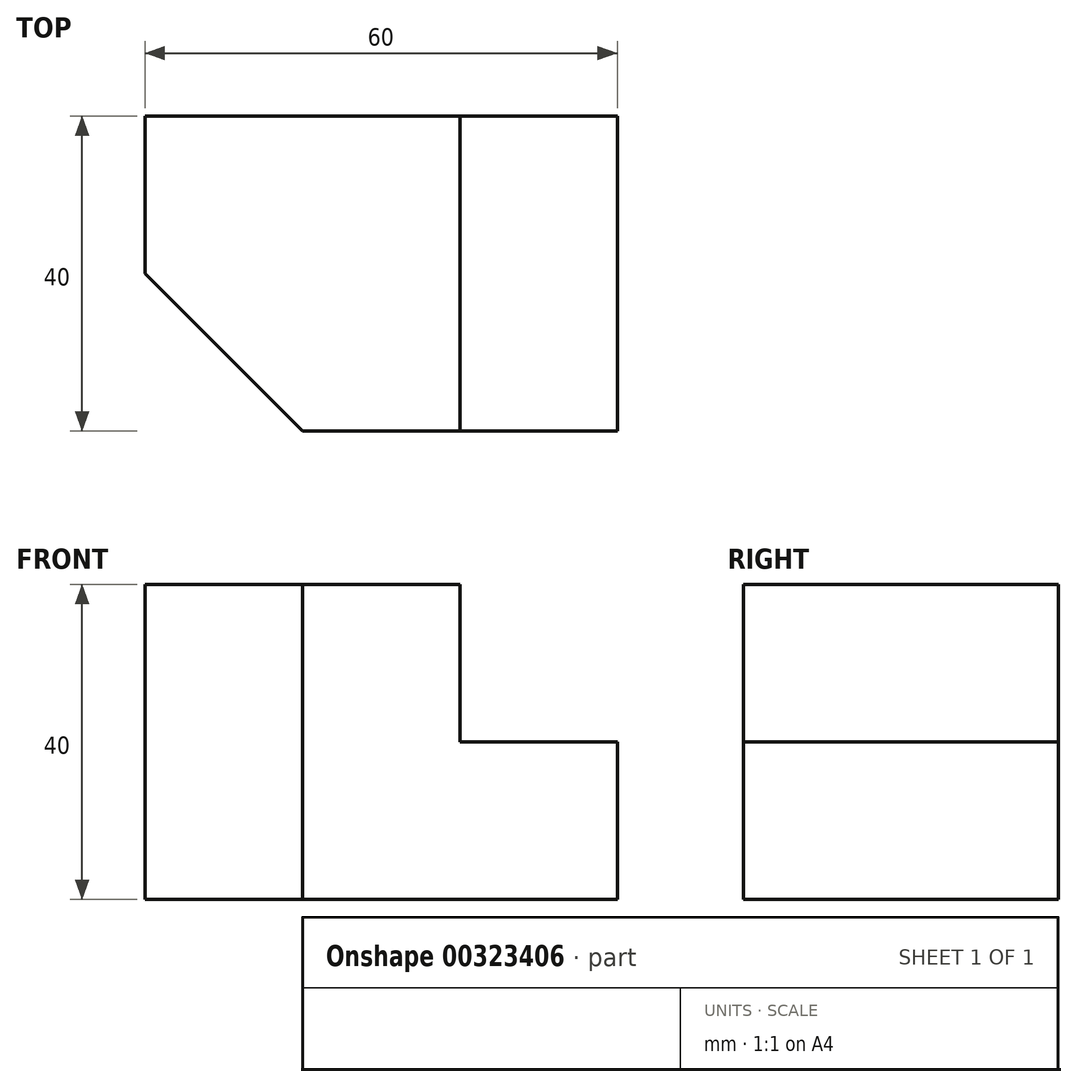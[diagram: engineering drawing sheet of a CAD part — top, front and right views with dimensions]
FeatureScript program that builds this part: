
annotation { "Feature Type Name" : "Feature", "Feature Type Description" : "" }
export const myFeature = defineFeature(function(context is Context, id is Id, definition is map)
    precondition{}
    {
        {
            var Q0;
            Q0=qCreatedBy(makeId("Front.planeOp"),FACE);
            var sketch = newSketch(context, id + "F0", { "sketchPlane" : qUnion([Q0])});
            skLineSegment(sketch, "E0.bottom", {"start": v(0, 0) * mm, "end": v(60, 0) * mm});
            skLineSegment(sketch, "E0.top", {"start": v(0, 40) * mm, "end": v(60, 40) * mm});
            skLineSegment(sketch, "E0.left", {"start": v(0, 0) * mm, "end": v(0, 40) * mm});
            skLineSegment(sketch, "E0.right", {"start": v(60, 0) * mm, "end": v(60, 40) * mm});
            skSolve(sketch);
        }
        {
            var Q0;
            Q0 = qSketchRegion(id + "F0", true);
            extrude(context, id + "F1", {"entities" : qUnion([Q0]), "oppositeDirection" : true, "depth" : 40 * mm});
        }
        {
            var Q0;
            Q0=makeQuery(id+"F1.opExtrude","CAP_FACE",FACE,{"disambiguationData":[OSD([sQuery(id+"F0.wireOp",EDGE,"E0.bottom"),sQuery(id+"F0.wireOp",EDGE,"E0.top"),sQuery(id+"F0.wireOp",EDGE,"E0.left"),sQuery(id+"F0.wireOp",EDGE,"E0.right")])],"isStart":true});
            var sketch = newSketch(context, id + "F2", { "sketchPlane" : qUnion([Q0])});
            skLineSegment(sketch, "E1.bottom", {"start": v(60, 40) * mm, "end": v(40, 40) * mm});
            skLineSegment(sketch, "E1.top", {"start": v(60, 20) * mm, "end": v(40, 20) * mm});
            skLineSegment(sketch, "E1.left", {"start": v(60, 40) * mm, "end": v(60, 20) * mm});
            skLineSegment(sketch, "E1.right", {"start": v(40, 40) * mm, "end": v(40, 20) * mm});
            skSolve(sketch);
        }
        {
            var Q0;
            Q0 = qSketchRegion(id + "F2", true);
            extrude(context, id + "F3", {"entities" : qUnion([Q0]), "operationType" : NewBodyOperationType.REMOVE, "endBound" : BoundingType.THROUGH_ALL, "oppositeDirection" : true, "depth" : 25 * mm});
        }
        {
            var Q0;
            Q0=makeQuery(id+"F1.opExtrude","SWEPT_FACE",FACE,{"disambiguationData":[OSD([sQuery(id+"F0.wireOp",EDGE,"E0.top")])]});
            var sketch = newSketch(context, id + "F4", { "sketchPlane" : qUnion([Q0])});
            skLineSegment(sketch, "E2", {"start": v(0, 20) * mm, "end": v(0, 0) * mm});
            skLineSegment(sketch, "E3", {"start": v(0, 0) * mm, "end": v(20, 0) * mm});
            skLineSegment(sketch, "E4", {"start": v(20, 0) * mm, "end": v(0, 20) * mm});
            skSolve(sketch);
        }
        {
            var Q0;
            Q0 = qSketchRegion(id + "F4", true);
            extrude(context, id + "F5", {"entities" : qUnion([Q0]), "operationType" : NewBodyOperationType.REMOVE, "endBound" : BoundingType.THROUGH_ALL, "oppositeDirection" : true, "depth" : 25 * mm});
        }
    });
